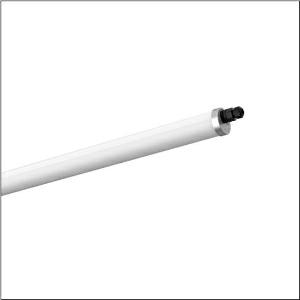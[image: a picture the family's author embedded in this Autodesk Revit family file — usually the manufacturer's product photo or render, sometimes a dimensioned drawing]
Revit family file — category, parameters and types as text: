
# Revit family: monsun_r__31_tube_51ft10dn4a0a_ff33
name_source: partatom
category: Lighting Fixtures
units: mm (PartAtom-declared; Revit-internal decimal feet)

## family parameters
Cut with Voids When Loaded = No
Host = Face
Light Source = No
Part Type = Normal
Room Calculation Point = No
Round Connector Dimension = Use Diameter
Shared = No

## types (1)
- Monsun® 31 Tube (1 x LED, 10000 lm, 58 W, 4000K)
    Apparent Load = 58 VA
    CIE Flux Codes = 42 71 90 91 100
    Color Rendering = 80
    Color Temperature = 4000K
    Default Elevation = 1800 mm
    Description = Monsun® 31 Tube, tubular luminaire, primary optical cover: diffuser, of PMMA, light emission: direct distribution, primary light characteristic: symmetric, installation type: suspended mounting, surface-mounted, LED, rated luminous flux: 10.000lm, luminous efficacy: 160lm/W, light colour: 840, colour temperature: 4000K, with with 1 terminal, 5-pole, max. 2.5mm², through-wiring: 5x 1.5mm², mains connection: 220..240V, AC, 50/60Hz, rated input power: 58W, housing, cylindrical, of PMMA, semi-transparent, matt white, with luminaire and ceiling fastening, V4A, mounting with brackets of stainless steel, length: 1.570mm, diameter: 75mm, end cap, of stainless steel (V4A), protection rating (complete): IP67/IP69K, insulation class (complete): insulation class I (protective earthing), certification: CE, UKCA, impact resistance: IK07, permissible operating ambient temperature: -20..+40°C, corresponds to IFS (International Featured Standards) requirements for safety and quality in the food industry, usage in unprotected outdoor area possible with horizontal mounting, contact your sales advisor before using the luminaires in applications with unclear chemical exposure, large temperature fluctuations or condensation-forming humidity, packaging unit: 1 piece
    Height = 83 mm
    Lamp = 1 x LED
    Lamp Light Flux = 10000 lm
    Lamp Power = 58 W
    Lamp count = 1
    Length = 1570 mm
    Luminous efficacy = 172 lm/W
    Manufacturer = Siteco
    ModVariant = No
    Model = 51FT10DN4A0A
    Mounting Place = Ceiling
    Mounting Type = Pendant
    Number of Poles = 1
    OnlyDefault = Yes
    Power Factor = 1
    Product Name = Monsun® 31 Tube
    Product group = tubular luminaire
    ProductGroupID = 906
    Protection Class = Protection class I
    RLX_Detail_Level = 1
    RLX_Emergency_Light_Flux = 0 lm
    RLX_Emergency_Type = 0
    RLX_Emergency_Type_DB = No
    RlxData = <blob elided: 25361 chars, md5=7dacdf31>
    Socket = socket
    Standby Power = 0 W
    System Light Flux = 10000 lm
    System Power = 58 W
    Type Comments = Product without accessories
    Type Image = l_1228461.jpg
    URL = http://relux.com
    VarID = ---
    Voltage = 0 V
    Weight = 0.00 kg
    Width = 75 mm

## geometry (parser evidence)
native form markers: Blend x4, Sweep x12
no freeform markers — native parametric forms only
